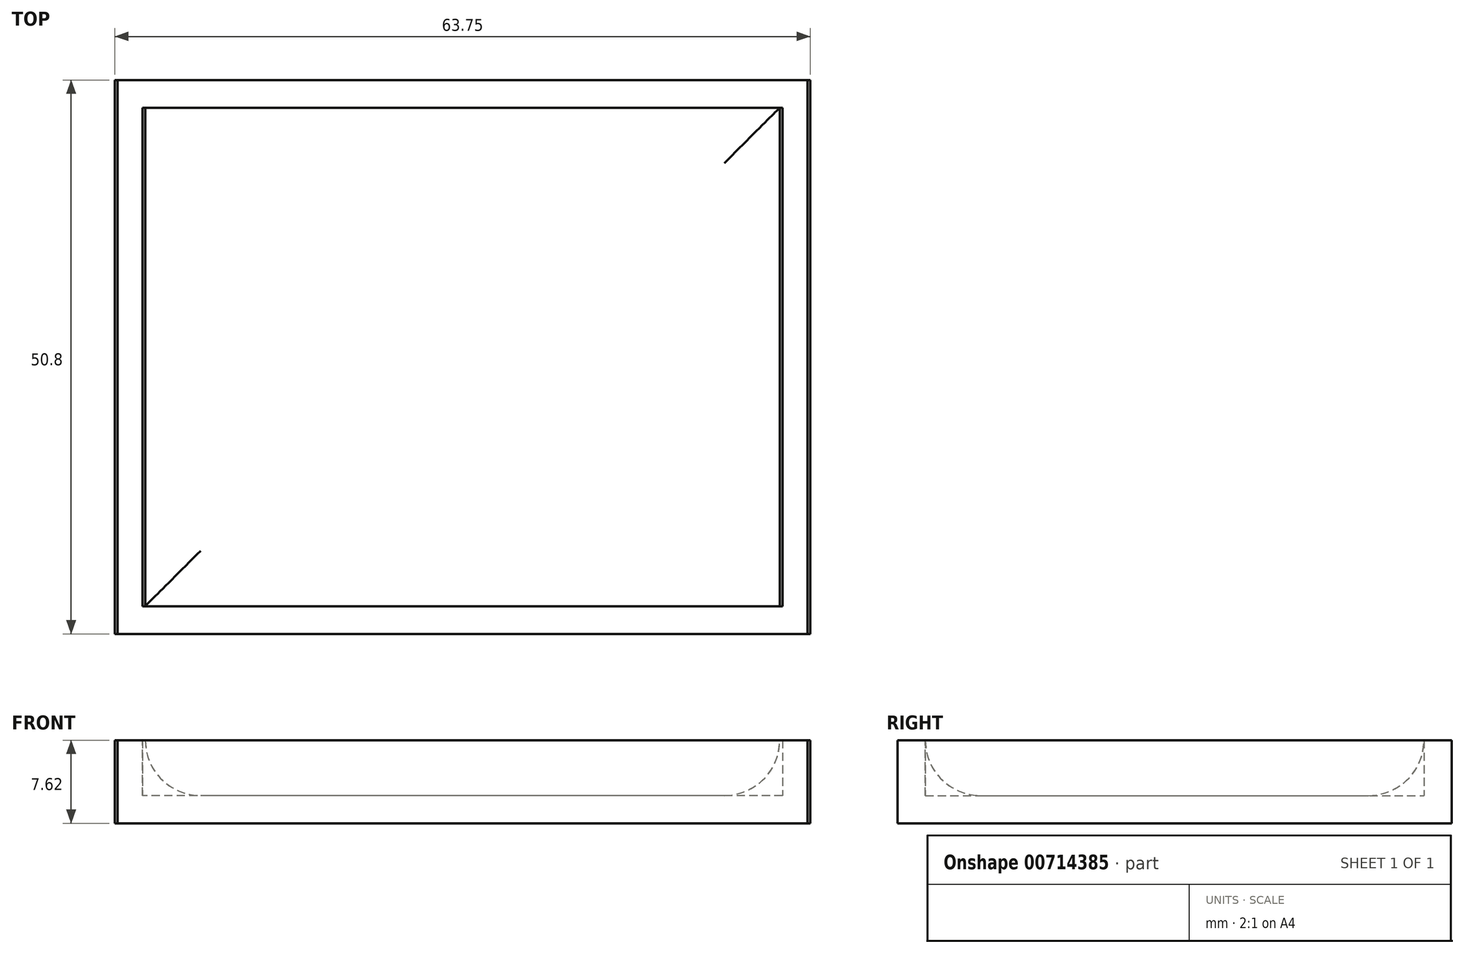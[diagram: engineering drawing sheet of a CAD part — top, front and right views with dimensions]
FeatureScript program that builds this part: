
annotation { "Feature Type Name" : "Feature", "Feature Type Description" : "" }
export const myFeature = defineFeature(function(context is Context, id is Id, definition is map)
    precondition{}
    {
        {
            var Q0;
            Q0=qCreatedBy(makeId("Front.planeOp"),FACE);
            var sketch = newSketch(context, id + "F0", { "sketchPlane" : qUnion([Q0])});
            skLineSegment(sketch, "E0.bottom", {"start": v(29.6, -7.44) * mm, "end": v(-33.9, -7.44) * mm});
            skLineSegment(sketch, "E0.top", {"start": v(29.6, -15.06) * mm, "end": v(-33.9, -15.06) * mm});
            skLineSegment(sketch, "E0.left", {"start": v(29.6, -7.44) * mm, "end": v(29.6, -15.06) * mm});
            skLineSegment(sketch, "E0.right", {"start": v(-33.9, -7.44) * mm, "end": v(-33.9, -15.06) * mm});
            skSolve(sketch);
        }
        {
            var Q0;
            Q0 = qSketchRegion(id + "F0", true);
            extrude(context, id + "F1", {"entities" : qUnion([Q0]), "endBound" : BoundingType.SYMMETRIC, "depth" : 50.8 * mm, "offsetDistance" : 25.4 * mm});
        }
        {
            var Q0;
            Q0=makeQuery(id+"F1.opExtrude","SWEPT_FACE",FACE,{"disambiguationData":[OSD([sQuery(id+"F0.wireOp",EDGE,"E0.bottom")])]});
            shell(context, id + "F2", {"entities" : qUnion([Q0]), "thickness" : 2.54 * mm});
        }
        {
            var Q0;
            Q0=makeQuery(id+"F1.opExtrude","SWEPT_BODY",BODY,{"disambiguationData":[OSD([sQuery(id+"F0.wireOp",EDGE,"E0.bottom"),sQuery(id+"F0.wireOp",EDGE,"E0.top"),sQuery(id+"F0.wireOp",EDGE,"E0.left"),sQuery(id+"F0.wireOp",EDGE,"E0.right")])]});
            transform(context, id + "F3", {"entities" : qUnion([Q0]), "transformType" : TransformType.TRANSLATION_3D, "dx" : -0.25 * mm, "dy" : 0 * mm, "dz" : 0 * mm, "makeCopy" : true});
        }
        {
            var Q0;
            Q0=makeQuery(id+"F2.opShell","OFFSET_EDGE",EDGE,{"disambiguationData":[OSD([sQuery(id+"F0.wireOp",EDGE,"E0.top"),sQuery(id+"F0.wireOp",EDGE,"E0.right")])]});
            var Q1;
            {var subQ0=sQuery(id+"F0.wireOp",EDGE,"E0.top");Q1=makeQuery(id+"F3.opPattern","COPY",EDGE,{"derivedFrom":makeQuery(id+"F2.opShell","OFFSET_EDGE",EDGE,{"disambiguationData":[OSD([subQ0]),TDD([makeQuery(id+"F1.opExtrude","CAP_EDGE",EDGE,{"disambiguationData":[OSD([subQ0])],"isStart":true})])]}),"instanceName":"1"});}
            var Q2;
            Q2=makeQuery(id+"F3.opPattern","COPY",EDGE,{"derivedFrom":makeQuery(id+"F2.opShell","OFFSET_EDGE",EDGE,{"disambiguationData":[OSD([sQuery(id+"F0.wireOp",EDGE,"E0.top"),sQuery(id+"F0.wireOp",EDGE,"E0.left")])]}),"instanceName":"1"});
            var Q3;
            {var subQ0=sQuery(id+"F0.wireOp",EDGE,"E0.top");Q3=makeQuery(id+"F2.opShell","OFFSET_EDGE",EDGE,{"disambiguationData":[OSD([subQ0]),TDD([makeQuery(id+"F1.opExtrude","CAP_EDGE",EDGE,{"disambiguationData":[OSD([subQ0])],"isStart":false})])]});}
            fillet(context, id + "F4", {"entities" : qUnion([Q0, Q1, Q2, Q3]), "radius" : 5.08 * mm, "tangentPropagation" : true, "allowEdgeOverflow" : false});
        }
    });
